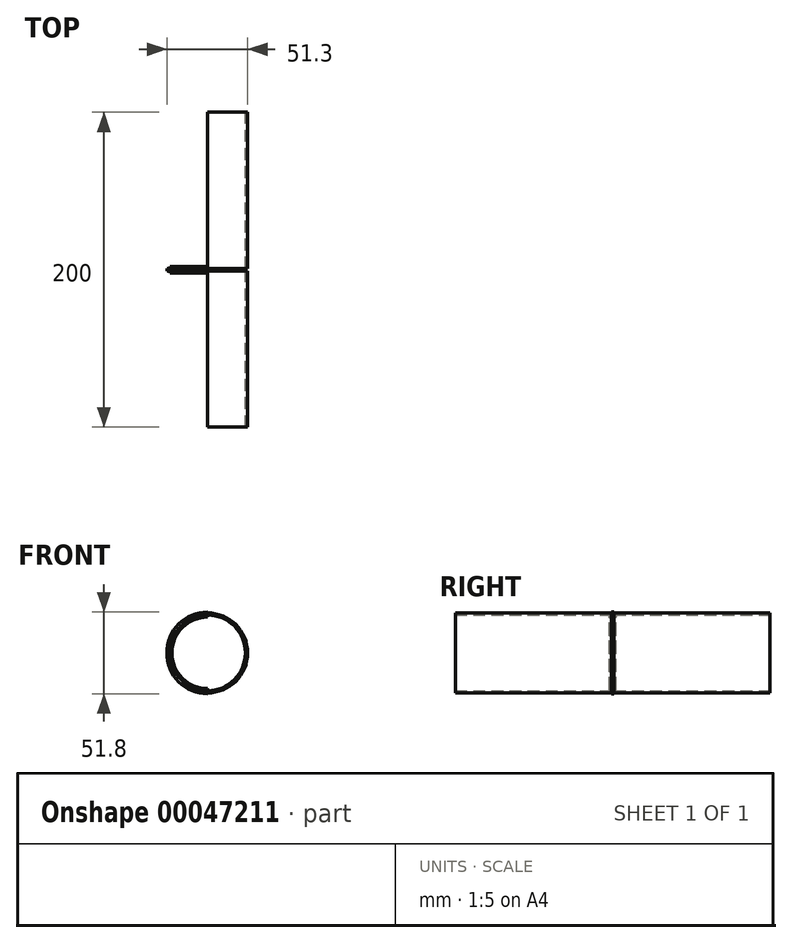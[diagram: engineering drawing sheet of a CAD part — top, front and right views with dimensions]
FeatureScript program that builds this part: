
annotation { "Feature Type Name" : "Feature", "Feature Type Description" : "" }
export const myFeature = defineFeature(function(context is Context, id is Id, definition is map)
    precondition{}
    {
        {
            var Q0;
            Q0=qCreatedBy(makeId("Front.planeOp"),FACE);
            var sketch = newSketch(context, id + "F0", { "sketchPlane" : qUnion([Q0])});
            skCircle(sketch, "E0", {"center": v(0, 0) * mm, "radius": 25.4 * mm});
            skCircle(sketch, "E1.0", {"center": v(0, 0) * mm, "radius": 24 * mm});
            skLineSegment(sketch, "E2", {"start": v(0, 30.7) * mm, "end": v(0, -32.6) * mm});
            skSolve(sketch);
        }
        {
            var Q0;
            {var subQ0=sQuery(id+"F0.wireOp",EDGE,"E2");var subQ3=sQuery(id+"F0.wireOp",EDGE,"E0");var subQ6=makeQuery(id+"F0.imprint","INTERSECT",VERTEX,{"disambiguationData":[OD(0.0)],"derivedFrom":[subQ3,subQ0]});Q0=makeQuery(id+"F0.imprint","IMPRINT",FACE,{"disambiguationData":[TD([[makeQuery(id+"F0.imprint","IMPRINT",EDGE,{"disambiguationData":[TD([[subQ6,-1.0]])],"derivedFrom":subQ3}),1.0]])]});}
            extrude(context, id + "F1", {"entities" : qUnion([Q0]), "endBound" : BoundingType.SYMMETRIC, "depth" : 200 * mm});
        }
        {
            var Q0;
            Q0=qCreatedBy(makeId("Front.planeOp"),FACE);
            var sketch = newSketch(context, id + "F2", { "sketchPlane" : qUnion([Q0])});
            skCircle(sketch, "E3.0", {"center": v(0, 0) * mm, "radius": 25.4 * mm});
            skSolve(sketch);
        }
        {
            var Q0;
            Q0 = qSketchRegion(id + "F2", true);
            extrude(context, id + "F3", {"entities" : qUnion([Q0]), "operationType" : NewBodyOperationType.REMOVE, "endBound" : BoundingType.SYMMETRIC, "oppositeDirection" : true, "depth" : 1.5 * mm});
        }
        {
            var Q0;
            Q0=qCreatedBy(makeId("Right.planeOp"),FACE);
            var sketch = newSketch(context, id + "F4", { "sketchPlane" : qUnion([Q0])});
            skLineSegment(sketch, "E4.0", {"start": v(-0.75, 25.9) * mm, "end": v(-0.75, 24) * mm});
            skLineSegment(sketch, "E4.1", {"start": v(0.75, 25.9) * mm, "end": v(0.75, 24) * mm});
            skPoint(sketch, "E5.orphan", {"position": v(-0.75, 25.4) * mm});
            skPoint(sketch, "E6.orphan", {"position": v(0.75, 25.4) * mm});
            skLineSegment(sketch, "E7", {"start": v(-0.75, 25.9) * mm, "end": v(0.75, 25.9) * mm});
            skLineSegment(sketch, "E8", {"start": v(-2, 23.7) * mm, "end": v(-2, 22.7) * mm});
            skLineSegment(sketch, "E9", {"start": v(-2, 22.7) * mm, "end": v(2, 22.7) * mm});
            skLineSegment(sketch, "E10.MirrorCS", {"start": v(2, 23.7) * mm, "end": v(2, 22.7) * mm});
            skLineSegment(sketch, "E11.0", {"start": v(-1.48, 24) * mm, "end": v(-0.75, 24) * mm});
            skLineSegment(sketch, "E11.1", {"start": v(0.75, 24) * mm, "end": v(1.48, 24) * mm});
            skPoint(sketch, "E12.orphan", {"position": v(-100, 24) * mm});
            skPoint(sketch, "E13.orphan", {"position": v(100, 24) * mm});
            skLineSegment(sketch, "E14", {"start": v(-2, 23.7) * mm, "end": v(-1.48, 24) * mm});
            skLineSegment(sketch, "E15.MirrorCS", {"start": v(2, 23.7) * mm, "end": v(1.48, 24) * mm});
            skLineSegment(sketch, "E16", {"start": v(0, 0) * mm, "end": v(15.22, 0) * mm, "construction": true});
            skLineSegment(sketch, "E17.0", {"start": v(0.75, 25.4) * mm, "end": v(100, 25.4) * mm});
            skSolve(sketch);
        }
        {
            var Q0;
            {var subQ3=sQuery(id+"F4.wireOp",EDGE,"E4.0");Q0=makeQuery(id+"F4.imprint","IMPRINT",FACE,{"disambiguationData":[TD([[makeQuery(id+"F4.imprint","IMPRINT",EDGE,{"derivedFrom":subQ3}),1.0]])]});}
            var Q1;
            {var subQ0=sQuery(id+"F0.wireOp",EDGE,"E1.0");Q1=makeQuery(id+"F3.boolean.opBoolean","SPLIT",FACE,{"disambiguationData":[TD([makeQuery(id+"F3.opExtrude","CAP_FACE",FACE,{"disambiguationData":[OSD([sQuery(id+"F2.wireOp",EDGE,"E3.0")])],"isStart":false})])],"derivedFrom":makeQuery(id+"F1.opExtrude","SWEPT_FACE",FACE,{"disambiguationData":[OSD([subQ0])]})});}
            revolve(context, id + "F5", {"entities" : qUnion([Q0]), "axis" : qUnion([Q1]), "revolveType" : RevolveType.ONE_DIRECTION, "angle" : 180 * degree});
        }
    });
